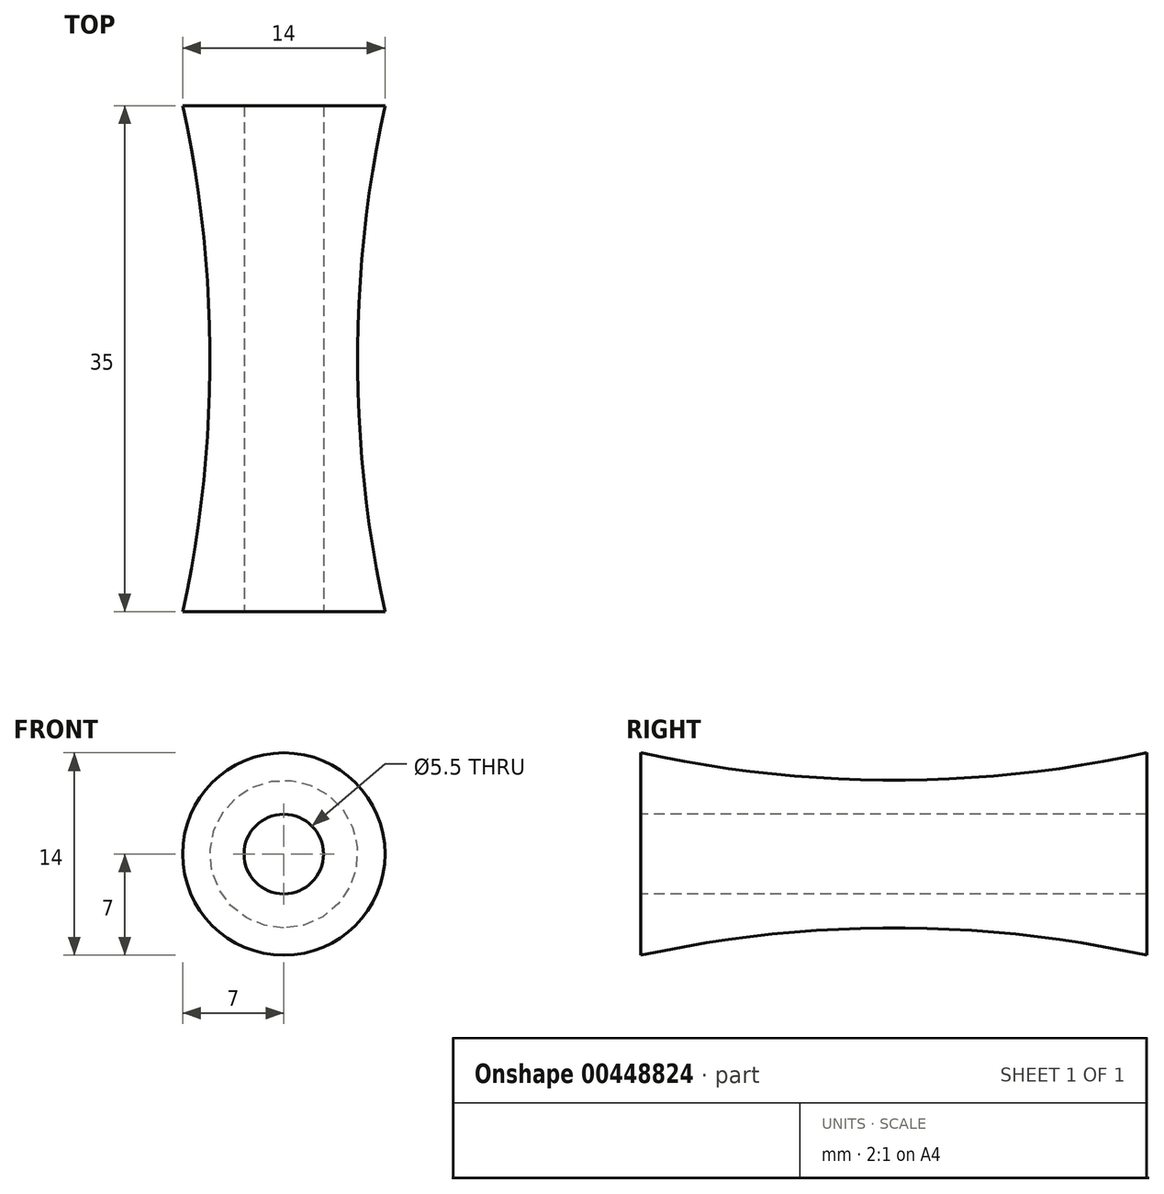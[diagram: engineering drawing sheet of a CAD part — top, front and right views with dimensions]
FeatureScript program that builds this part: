
annotation { "Feature Type Name" : "Feature", "Feature Type Description" : "" }
export const myFeature = defineFeature(function(context is Context, id is Id, definition is map)
    precondition{}
    {
        {
            var Q0;
            Q0=qCreatedBy(makeId("Top.planeOp"),FACE);
            var sketch = newSketch(context, id + "F0", { "sketchPlane" : qUnion([Q0])});
            skLineSegment(sketch, "E0", {"start": v(0, 0) * mm, "end": v(0, 35) * mm});
            skLineSegment(sketch, "E1", {"start": v(0, 35) * mm, "end": v(7, 35) * mm, "construction": true});
            skLineSegment(sketch, "E2", {"start": v(7, 35) * mm, "end": v(7, 0) * mm, "construction": true});
            skLineSegment(sketch, "E3", {"start": v(7, 0) * mm, "end": v(0, 0) * mm, "construction": true});
            skLineSegment(sketch, "E4", {"start": v(2.75, 35) * mm, "end": v(2.75, 0) * mm});
            skArc(sketch, "E5", {"start": v(7, 35) * mm, "mid": v(5.1, 17.5) * mm, "end": v(7, 0) * mm});
            skPoint(sketch, "E5.centerSnap0", {"position": v(7, 17.5) * mm});
            skLineSegment(sketch, "E6", {"start": v(2.75, 35) * mm, "end": v(7, 35) * mm});
            skLineSegment(sketch, "E7", {"start": v(2.75, 0) * mm, "end": v(7, 0) * mm});
            skSolve(sketch);
        }
        {
            var Q0;
            Q0=makeQuery(id+"F0.imprint","IMPRINT",FACE,{"disambiguationData":[TD([[makeQuery(id+"F0.imprint","IMPRINT",EDGE,{"derivedFrom":sQuery(id+"F0.wireOp",EDGE,"E4")}),1.0]])]});
            var Q1;
            Q1=sQuery(id+"F0.wireOp",EDGE,"E0");
            revolve(context, id + "F1", {"surfaceOperationType" : NewSurfaceOperationType.NEW, "entities" : qUnion([Q0]), "axis" : qUnion([Q1]), "revolveType" : RevolveType.FULL});
        }
    });
